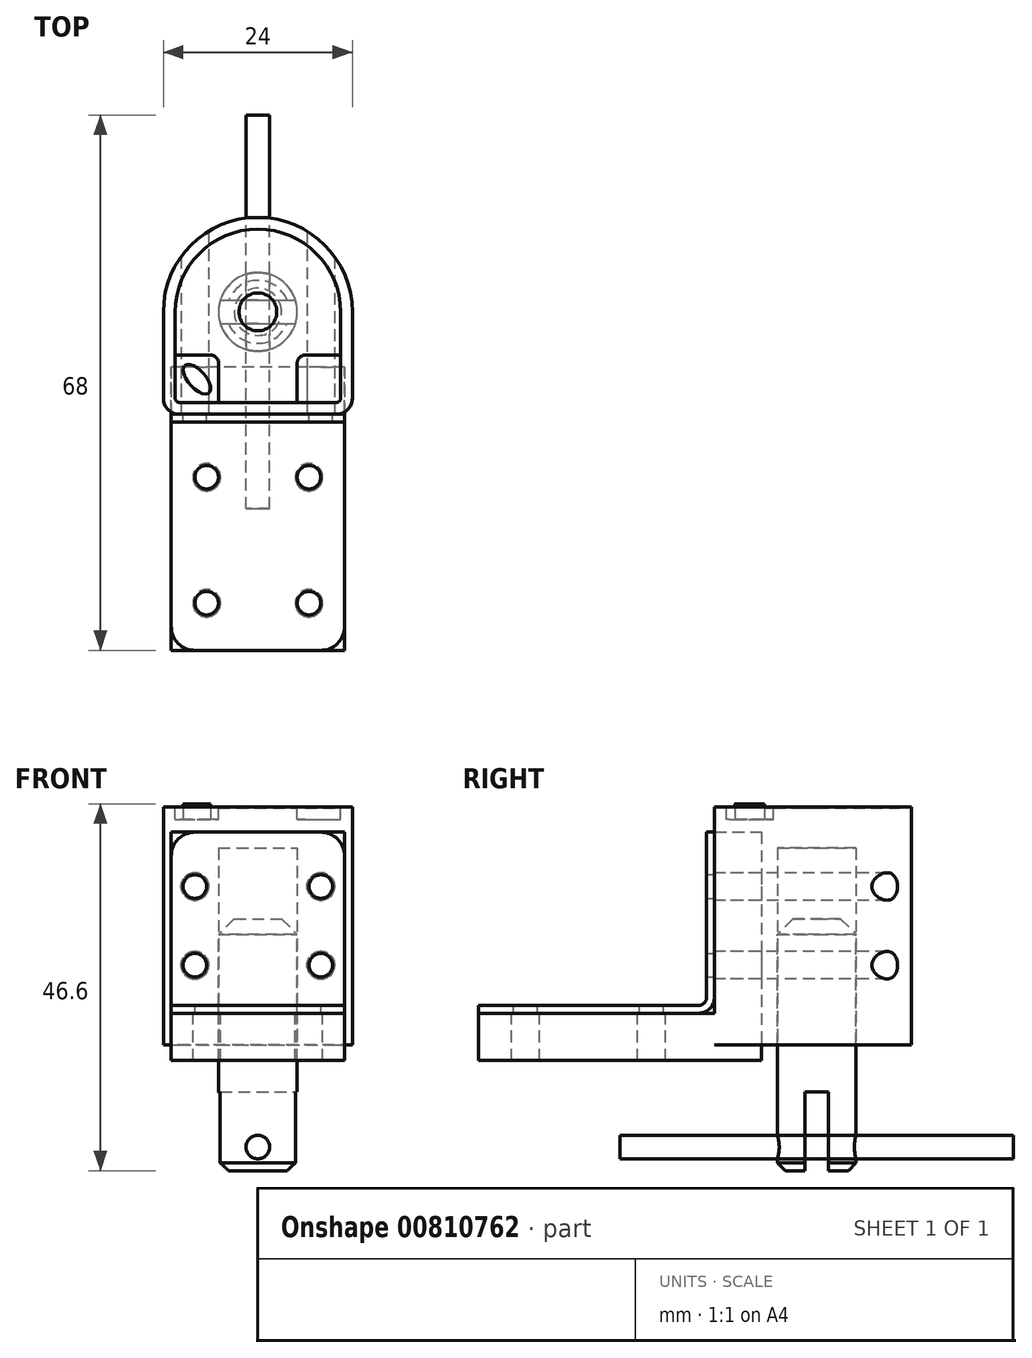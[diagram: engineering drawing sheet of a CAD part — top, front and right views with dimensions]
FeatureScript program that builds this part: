
annotation { "Feature Type Name" : "Feature", "Feature Type Description" : "" }
export const myFeature = defineFeature(function(context is Context, id is Id, definition is map)
    precondition{}
    {
        {
            var Q0;
            Q0=qCreatedBy(makeId("Top.planeOp"),FACE);
            var sketch = newSketch(context, id + "F0", { "sketchPlane" : qUnion([Q0])});
            skArc(sketch, "E0", {"start": v(12, 0) * mm, "mid": v(0, 12) * mm, "end": v(-12, 0) * mm});
            skLineSegment(sketch, "E1", {"start": v(-12, 0) * mm, "end": v(-12, -13) * mm});
            skLineSegment(sketch, "E2", {"start": v(-12, -13) * mm, "end": v(12, -13) * mm});
            skLineSegment(sketch, "E3", {"start": v(12, -13) * mm, "end": v(12, 0) * mm});
            skLineSegment(sketch, "E4", {"start": v(0, 12) * mm, "end": v(0, -13) * mm, "construction": true});
            skSolve(sketch);
        }
        {
            var Q0;
            Q0=qSketchRegion(id+"F0",true);
            extrude(context, id + "F1", {"entities" : qUnion([Q0]), "oppositeDirection" : true, "depth" : 30.2 * mm});
        }
        {
            var Q0;
            Q0=makeQuery(id+"F1.opExtrude","CAP_FACE",FACE,{"disambiguationData":[OSD([sQuery(id+"F0.wireOp",EDGE,"E0"),sQuery(id+"F0.wireOp",EDGE,"E1"),sQuery(id+"F0.wireOp",EDGE,"E2"),sQuery(id+"F0.wireOp",EDGE,"E3")])],"isStart":false});
            var sketch = newSketch(context, id + "F2", { "sketchPlane" : qUnion([Q0])});
            skCircle(sketch, "E5", {"center": v(0, 0) * mm, "radius": 5 * mm});
            skSolve(sketch);
        }
        {
            var Q0;
            Q0=qSketchRegion(id+"F2",true);
            extrude(context, id + "F3", {"entities" : qUnion([Q0]), "operationType" : NewBodyOperationType.REMOVE, "oppositeDirection" : true, "depth" : 25 * mm});
        }
        {
            var Q0;
            Q0=qSketchRegion(id+"F2",true);
            extrude(context, id + "F4", {"entities" : qUnion([Q0]), "depth" : 32 * mm, "symmetric" : true});
        }
        {
            var Q0;
            Q0=makeQuery(id+"F1.opExtrude","SWEPT_EDGE",EDGE,{"disambiguationData":[OSD([sQuery(id+"F0.wireOp",EDGE,"E2"),sQuery(id+"F0.wireOp",EDGE,"E3")])]});
            var Q1;
            Q1=makeQuery(id+"F1.opExtrude","SWEPT_EDGE",EDGE,{"disambiguationData":[OSD([sQuery(id+"F0.wireOp",EDGE,"E1"),sQuery(id+"F0.wireOp",EDGE,"E2")])]});
            fillet(context, id + "F5", {"entities" : qUnion([Q0, Q1]), "radius" : 2 * mm, "tangentPropagation" : true, "allowEdgeOverflow" : false});
        }
        {
            var Q0;
            Q0=makeQuery(id+"F4.opExtrude","CAP_EDGE",EDGE,{"disambiguationData":[OSD([sQuery(id+"F2.wireOp",EDGE,"E5")])],"isStart":true});
            chamfer(context, id + "F6", {"entities" : qUnion([Q0]), "width" : 2 * mm, "tangentPropagation" : true});
        }
        {
            var Q0;
            Q0=makeQuery(id+"F4.opExtrude","CAP_EDGE",EDGE,{"disambiguationData":[OSD([sQuery(id+"F2.wireOp",EDGE,"E5")])],"isStart":false});
            chamfer(context, id + "F7", {"entities" : qUnion([Q0]), "width" : 1 * mm, "tangentPropagation" : true});
        }
        {
            var Q0;
            Q0=qCreatedBy(makeId("Right.planeOp"),FACE);
            var sketch = newSketch(context, id + "F8", { "sketchPlane" : qUnion([Q0])});
            skLineSegment(sketch, "E6.bottom", {"start": v(-1.5, -46.2) * mm, "end": v(1.5, -46.2) * mm});
            skLineSegment(sketch, "E6.top", {"start": v(-1.5, -36.2) * mm, "end": v(1.5, -36.2) * mm});
            skLineSegment(sketch, "E6.left", {"start": v(-1.5, -46.2) * mm, "end": v(-1.5, -36.2) * mm});
            skLineSegment(sketch, "E6.right", {"start": v(1.5, -46.2) * mm, "end": v(1.5, -36.2) * mm});
            skPoint(sketch, "E7", {"position": v(0, -46.2) * mm});
            skSolve(sketch);
        }
        {
            var Q0;
            Q0=qSketchRegion(id+"F8",true);
            extrude(context, id + "F9", {"entities" : qUnion([Q0]), "operationType" : NewBodyOperationType.REMOVE, "oppositeDirection" : true, "depth" : 25 * mm, "symmetric" : true});
        }
        {
            var Q0;
            Q0=qCreatedBy(makeId("Front.planeOp"),FACE);
            var sketch = newSketch(context, id + "F10", { "sketchPlane" : qUnion([Q0])});
            skCircle(sketch, "E8", {"center": v(0, -43.2) * mm, "radius": 1.5 * mm});
            skSolve(sketch);
        }
        {
            var Q0;
            Q0=qSketchRegion(id+"F10",true);
            extrude(context, id + "F11", {"entities" : qUnion([Q0]), "operationType" : NewBodyOperationType.REMOVE, "oppositeDirection" : true, "depth" : 25 * mm, "symmetric" : true});
        }
        {
            var Q0;
            Q0=qSketchRegion(id+"F10",true);
            extrude(context, id + "F12", {"entities" : qUnion([Q0]), "depth" : 50 * mm, "symmetric" : true});
        }
        {
            var Q0;
            Q0=makeQuery(id+"F1.opExtrude","CAP_FACE",FACE,{"disambiguationData":[OSD([sQuery(id+"F0.wireOp",EDGE,"E0"),sQuery(id+"F0.wireOp",EDGE,"E1"),sQuery(id+"F0.wireOp",EDGE,"E2"),sQuery(id+"F0.wireOp",EDGE,"E3")])],"isStart":true});
            var sketch = newSketch(context, id + "F13", { "sketchPlane" : qUnion([Q0])});
            skArc(sketch, "E9.0", {"start": v(-10.5, -11) * mm, "mid": v(-10.35, -11.35) * mm, "end": v(-10, -11.5) * mm});
            skArc(sketch, "E9.1", {"start": v(10, -11.5) * mm, "mid": v(10.35, -11.35) * mm, "end": v(10.5, -11) * mm});
            skLineSegment(sketch, "E9.2", {"start": v(10.5, -11) * mm, "end": v(10.5, 0) * mm});
            skLineSegment(sketch, "E9.3", {"start": v(-10, -11.5) * mm, "end": v(10, -11.5) * mm});
            skArc(sketch, "E9.4", {"start": v(10.5, 0) * mm, "mid": v(0, 10.5) * mm, "end": v(-10.5, 0) * mm});
            skLineSegment(sketch, "E9.5", {"start": v(-10.5, 0) * mm, "end": v(-10.5, -11) * mm});
            skCircle(sketch, "E10", {"center": v(0, 0) * mm, "radius": 2.4 * mm});
            skSolve(sketch);
        }
        {
            var Q0;
            Q0=qSketchRegion(id+"F13",true);
            extrude(context, id + "F14", {"entities" : qUnion([Q0]), "operationType" : NewBodyOperationType.REMOVE, "oppositeDirection" : true, "depth" : .1 * mm});
        }
        {
            var Q0;
            Q0=makeQuery(id+"F14.boolean.opBoolean","COPY",FACE,{"derivedFrom":makeQuery(id+"F14.opExtrude","CAP_FACE",FACE,{"disambiguationData":[OSD([sQuery(id+"F13.wireOp",EDGE,"E9.0"),sQuery(id+"F13.wireOp",EDGE,"E9.1"),sQuery(id+"F13.wireOp",EDGE,"E9.2"),sQuery(id+"F13.wireOp",EDGE,"E9.3"),sQuery(id+"F13.wireOp",EDGE,"E9.4"),sQuery(id+"F13.wireOp",EDGE,"E9.5"),sQuery(id+"F13.wireOp",EDGE,"E10")])],"isStart":false})});
            var sketch = newSketch(context, id + "F15", { "sketchPlane" : qUnion([Q0])});
            skLineSegment(sketch, "E11.left", {"start": v(-5, -6.5) * mm, "end": v(-5, -11.5) * mm});
            skLineSegment(sketch, "E11.right", {"start": v(5, -6.5) * mm, "end": v(5, -11.5) * mm});
            skLineSegment(sketch, "E12.trimOffspring", {"start": v(6, -5.5) * mm, "end": v(10.5, -5.5) * mm});
            skLineSegment(sketch, "E13", {"start": v(-6, -5.5) * mm, "end": v(-10.5, -5.5) * mm});
            skLineSegment(sketch, "E14.0", {"start": v(-10, -11.5) * mm, "end": v(-5, -11.5) * mm});
            skLineSegment(sketch, "E14.1", {"start": v(-10.5, -5.5) * mm, "end": v(-10.5, -11) * mm});
            skLineSegment(sketch, "E14.2", {"start": v(10.5, -11) * mm, "end": v(10.5, -5.5) * mm});
            skArc(sketch, "E14.3", {"start": v(10, -11.5) * mm, "mid": v(10.35, -11.35) * mm, "end": v(10.5, -11) * mm});
            skArc(sketch, "E14.4", {"start": v(-10.5, -11) * mm, "mid": v(-10.35, -11.35) * mm, "end": v(-10, -11.5) * mm});
            skPoint(sketch, "E15.orphan", {"position": v(-10.5, 0) * mm});
            skLineSegment(sketch, "E16.trimOffspring", {"start": v(5, -11.5) * mm, "end": v(10, -11.5) * mm});
            skPoint(sketch, "E17.orphan", {"position": v(10.5, 0) * mm});
            skPoint(sketch, "E18.visualSharp", {"position": v(-5, -5.5) * mm});
            skArc(sketch, "E18.filletArc", {"start": v(-5, -6.5) * mm, "mid": v(-5.3, -5.8) * mm, "end": v(-6, -5.5) * mm});
            skPoint(sketch, "E19.visualSharp", {"position": v(5, -5.5) * mm});
            skArc(sketch, "E19.filletArc", {"start": v(6, -5.5) * mm, "mid": v(5.3, -5.8) * mm, "end": v(5, -6.5) * mm});
            skLineSegment(sketch, "E20", {"start": v(-5, -11.5) * mm, "end": v(5, -11.5) * mm, "construction": true});
            skLineSegment(sketch, "E21", {"start": v(0, 0) * mm, "end": v(0, -11.5) * mm, "construction": true});
            skSolve(sketch);
        }
        {
            var Q0;
            Q0=qSketchRegion(id+"F15",true);
            extrude(context, id + "F16", {"entities" : qUnion([Q0]), "operationType" : NewBodyOperationType.REMOVE, "oppositeDirection" : true, "depth" : 1.5 * mm});
        }
        {
            var Q0;
            Q0=makeQuery(id+"F16.boolean.opBoolean","COPY",FACE,{"derivedFrom":makeQuery(id+"F16.opExtrude","CAP_FACE",FACE,{"disambiguationData":[OSD([sQuery(id+"F15.wireOp",EDGE,"E11.left"),sQuery(id+"F15.wireOp",EDGE,"E13"),sQuery(id+"F15.wireOp",EDGE,"E14.0"),sQuery(id+"F15.wireOp",EDGE,"E14.1"),sQuery(id+"F15.wireOp",EDGE,"E14.4"),sQuery(id+"F15.wireOp",EDGE,"E18.filletArc")])],"isStart":false})});
            var sketch = newSketch(context, id + "F17", { "sketchPlane" : qUnion([Q0])});
            skEllipse(sketch, "E22", {"center": v(-7.75, -8.54) * mm, "majorRadius": 2.32 * mm, "minorRadius": 1.1 * mm, "majorAxis": v(-0.66, 0.75)});
            skLineSegment(sketch, "E23", {"start": v(-7.75, -8.54) * mm, "end": v(0, 0) * mm, "construction": true});
            skSolve(sketch);
        }
        {
            var Q0;
            Q0=makeQuery(id+"F1.opExtrude","SWEPT_FACE",FACE,{"disambiguationData":[OSD([sQuery(id+"F0.wireOp",EDGE,"E2")])]});
            var sketch = newSketch(context, id + "F18", { "sketchPlane" : qUnion([Q0])});
            skLineSegment(sketch, "E24", {"start": v(0, 0) * mm, "end": v(0, -30.2) * mm, "construction": true});
            skLineSegment(sketch, "E25.bottom", {"start": v(8, -10.1) * mm, "end": v(-8, -10.1) * mm, "construction": true});
            skLineSegment(sketch, "E25.top", {"start": v(8, -20.1) * mm, "end": v(-8, -20.1) * mm, "construction": true});
            skLineSegment(sketch, "E25.left", {"start": v(8, -10.1) * mm, "end": v(8, -20.1) * mm, "construction": true});
            skLineSegment(sketch, "E25.right", {"start": v(-8, -10.1) * mm, "end": v(-8, -20.1) * mm, "construction": true});
            skPoint(sketch, "E25.middle", {"position": v(0, -15.1) * mm});
            skCircle(sketch, "E26", {"center": v(-8, -10.1) * mm, "radius": 1.5 * mm});
            skCircle(sketch, "E27", {"center": v(8, -10.1) * mm, "radius": 1.5 * mm});
            skCircle(sketch, "E28", {"center": v(-8, -20.1) * mm, "radius": 1.5 * mm});
            skCircle(sketch, "E29", {"center": v(8, -20.1) * mm, "radius": 1.5 * mm});
            skSolve(sketch);
        }
        {
            var Q0;
            Q0=qSketchRegion(id+"F18",true);
            extrude(context, id + "F19", {"entities" : qUnion([Q0]), "operationType" : NewBodyOperationType.REMOVE, "oppositeDirection" : true, "depth" : 3 * mm});
        }
        {
            var Q0;
            Q0=qSketchRegion(id+"F17",true);
            extrude(context, id + "F20", {"entities" : qUnion([Q0]), "operationType" : NewBodyOperationType.ADD, "depth" : 2 * mm});
        }
        {
            var Q0;
            Q0=qCreatedBy(makeId("Right.planeOp"),FACE);
            var sketch = newSketch(context, id + "F21", { "sketchPlane" : qUnion([Q0])});
            skLineSegment(sketch, "E30", {"start": v(-13, -3.2) * mm, "end": v(-13, -24.2) * mm});
            skLineSegment(sketch, "E31", {"start": v(-15, -26.2) * mm, "end": v(-43, -26.2) * mm});
            skPoint(sketch, "E32.visualSharp", {"position": v(-13, -26.2) * mm});
            skArc(sketch, "E32.filletArc", {"start": v(-15, -26.2) * mm, "mid": v(-13.59, -25.61) * mm, "end": v(-13, -24.2) * mm});
            skLineSegment(sketch, "E33.0", {"start": v(-14, -3.2) * mm, "end": v(-14, -24.2) * mm});
            skArc(sketch, "E33.1", {"start": v(-15, -25.2) * mm, "mid": v(-14.3, -24.9) * mm, "end": v(-14, -24.2) * mm});
            skLineSegment(sketch, "E33.2", {"start": v(-15, -25.2) * mm, "end": v(-43, -25.2) * mm});
            skLineSegment(sketch, "E34", {"start": v(-14, -3.2) * mm, "end": v(-13, -3.2) * mm});
            skLineSegment(sketch, "E35", {"start": v(-43, -25.2) * mm, "end": v(-43, -26.2) * mm});
            skSolve(sketch);
        }
        {
            var Q0;
            Q0=qSketchRegion(id+"F21",true);
            extrude(context, id + "F22", {"entities" : qUnion([Q0]), "depth" : 22 * mm, "symmetric" : true});
        }
        {
            var Q0;
            Q0=qSketchRegion(id+"F18",true);
            extrude(context, id + "F23", {"entities" : qUnion([Q0]), "operationType" : NewBodyOperationType.REMOVE, "depth" : 3 * mm});
        }
        {
            var Q0;
            Q0=makeQuery(id+"F22.opExtrude","SWEPT_FACE",FACE,{"disambiguationData":[OSD([sQuery(id+"F21.wireOp",EDGE,"E33.2")])]});
            var sketch = newSketch(context, id + "F24", { "sketchPlane" : qUnion([Q0])});
            skLineSegment(sketch, "E36.bottom", {"start": v(6.5, -37) * mm, "end": v(-6.5, -37) * mm, "construction": true});
            skLineSegment(sketch, "E36.top", {"start": v(6.5, -21) * mm, "end": v(-6.5, -21) * mm, "construction": true});
            skLineSegment(sketch, "E36.left", {"start": v(6.5, -37) * mm, "end": v(6.5, -21) * mm, "construction": true});
            skLineSegment(sketch, "E36.right", {"start": v(-6.5, -37) * mm, "end": v(-6.5, -21) * mm, "construction": true});
            skPoint(sketch, "E36.middle", {"position": v(0, -29) * mm});
            skCircle(sketch, "E37", {"center": v(6.5, -21) * mm, "radius": 1.5 * mm});
            skCircle(sketch, "E38", {"center": v(6.5, -37) * mm, "radius": 1.5 * mm});
            skCircle(sketch, "E39", {"center": v(-6.5, -37) * mm, "radius": 1.5 * mm});
            skCircle(sketch, "E40", {"center": v(-6.5, -21) * mm, "radius": 1.5 * mm});
            skLineSegment(sketch, "E41", {"start": v(-11, -29) * mm, "end": v(11, -29) * mm, "construction": true});
            skSolve(sketch);
        }
        {
            var Q0;
            Q0=qSketchRegion(id+"F24",true);
            var Q1;
            Q1=sQuery(id+"F24.wireOp",EDGE,"E37");
            extrude(context, id + "F25", {"entities" : qUnion([Q0]), "operationType" : NewBodyOperationType.REMOVE, "surfaceEntities" : qUnion([Q1]), "oppositeDirection" : true, "depth" : 25 * mm});
        }
        {
            var Q0;
            Q0=makeQuery(id+"F22.opExtrude","CAP_EDGE",EDGE,{"disambiguationData":[OSD([sQuery(id+"F21.wireOp",EDGE,"E34")])],"isStart":true});
            var Q1;
            Q1=makeQuery(id+"F22.opExtrude","CAP_EDGE",EDGE,{"disambiguationData":[OSD([sQuery(id+"F21.wireOp",EDGE,"E34")])],"isStart":false});
            var Q2;
            Q2=makeQuery(id+"F22.opExtrude","CAP_EDGE",EDGE,{"disambiguationData":[OSD([sQuery(id+"F21.wireOp",EDGE,"E35")])],"isStart":false});
            var Q3;
            Q3=makeQuery(id+"F22.opExtrude","CAP_EDGE",EDGE,{"disambiguationData":[OSD([sQuery(id+"F21.wireOp",EDGE,"E35")])],"isStart":true});
            fillet(context, id + "F26", {"entities" : qUnion([Q0, Q1, Q2, Q3]), "radius" : 3 * mm, "tangentPropagation" : true, "allowEdgeOverflow" : false});
        }
        {
            var Q0;
            Q0=qCreatedBy(makeId("Right.planeOp"),FACE);
            var sketch = newSketch(context, id + "F27", { "sketchPlane" : qUnion([Q0])});
            skLineSegment(sketch, "E42", {"start": v(-43, -26.2) * mm, "end": v(-13, -26.2) * mm});
            skLineSegment(sketch, "E43", {"start": v(-13, -26.2) * mm, "end": v(-13, -3.2) * mm});
            skLineSegment(sketch, "E44", {"start": v(-13, -3.2) * mm, "end": v(-7, -3.2) * mm});
            skLineSegment(sketch, "E45", {"start": v(-7, -3.2) * mm, "end": v(-7, -32.2) * mm});
            skLineSegment(sketch, "E46", {"start": v(-7, -32.2) * mm, "end": v(-43, -32.2) * mm});
            skLineSegment(sketch, "E47", {"start": v(-43, -32.2) * mm, "end": v(-43, -26.2) * mm});
            skSolve(sketch);
        }
        {
            var Q0;
            Q0=qSketchRegion(id+"F27",true);
            extrude(context, id + "F28", {"entities" : qUnion([Q0]), "depth" : 22 * mm, "symmetric" : true});
        }
        {
            var Q0;
            Q0=makeQuery(id+"F28.opExtrude","SWEPT_FACE",FACE,{"disambiguationData":[OSD([sQuery(id+"F27.wireOp",EDGE,"E42")])]});
            var sketch = newSketch(context, id + "F29", { "sketchPlane" : qUnion([Q0])});
            skCircle(sketch, "E48", {"center": v(-6.5, -21) * mm, "radius": 1.75 * mm});
            skCircle(sketch, "E49", {"center": v(6.5, -21) * mm, "radius": 1.75 * mm});
            skCircle(sketch, "E50", {"center": v(-6.5, -37) * mm, "radius": 1.75 * mm});
            skCircle(sketch, "E51", {"center": v(6.5, -37) * mm, "radius": 1.75 * mm});
            skSolve(sketch);
        }
        {
            var Q0;
            Q0=qSketchRegion(id+"F29",true);
            extrude(context, id + "F30", {"entities" : qUnion([Q0]), "operationType" : NewBodyOperationType.REMOVE, "oppositeDirection" : true, "depth" : 25 * mm});
        }
        {
            var Q0;
            Q0=makeQuery(id+"F28.opExtrude","SWEPT_FACE",FACE,{"disambiguationData":[OSD([sQuery(id+"F27.wireOp",EDGE,"E43")])]});
            var sketch = newSketch(context, id + "F31", { "sketchPlane" : qUnion([Q0])});
            skCircle(sketch, "E52", {"center": v(-8, -10.1) * mm, "radius": 1.75 * mm});
            skCircle(sketch, "E53", {"center": v(8, -10.1) * mm, "radius": 1.75 * mm});
            skCircle(sketch, "E54", {"center": v(8, -20.1) * mm, "radius": 1.75 * mm});
            skCircle(sketch, "E55", {"center": v(-8, -20.1) * mm, "radius": 1.75 * mm});
            skSolve(sketch);
        }
        {
            var Q0;
            Q0=qSketchRegion(id+"F31",true);
            extrude(context, id + "F32", {"entities" : qUnion([Q0]), "operationType" : NewBodyOperationType.REMOVE, "oppositeDirection" : true, "depth" : 25 * mm});
        }
    });
